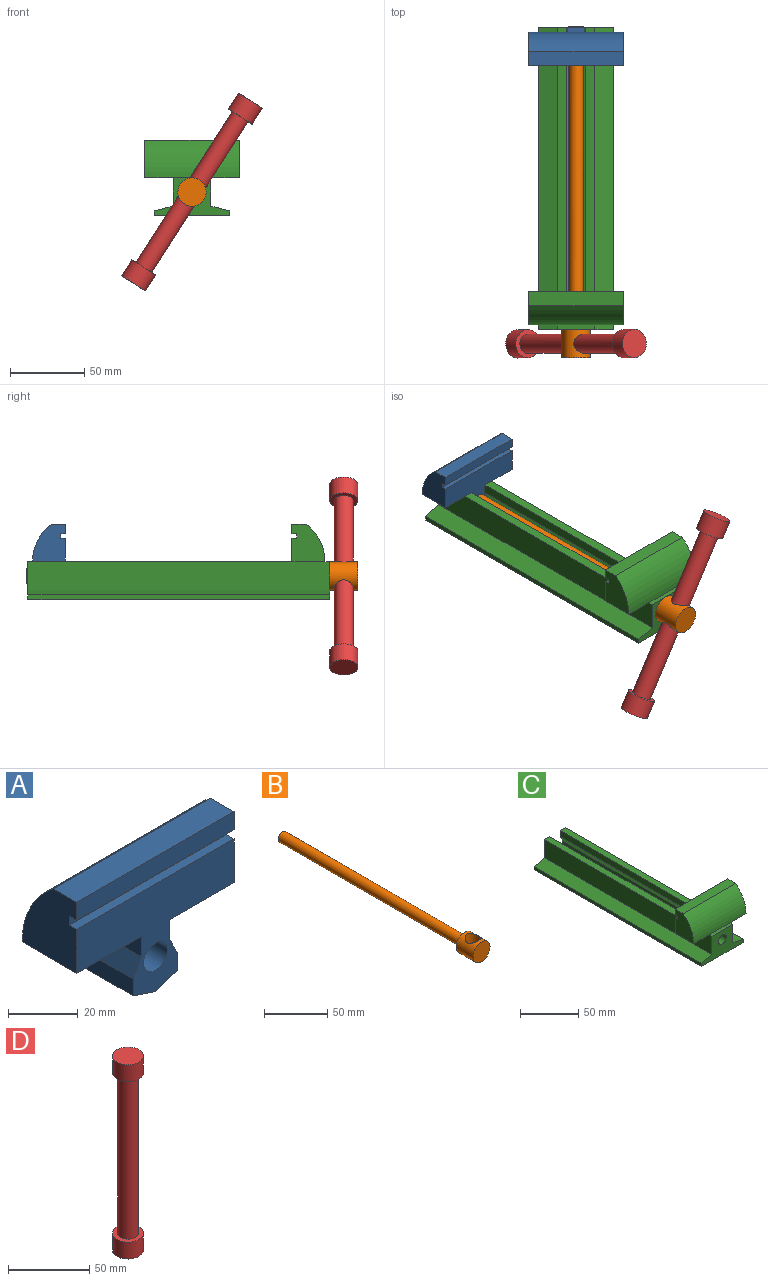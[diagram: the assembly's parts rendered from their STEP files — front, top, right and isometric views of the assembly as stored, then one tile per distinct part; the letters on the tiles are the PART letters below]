
ASSEMBLY  parts=4 mates=4
PART A: 22 faces, bbox 63.5x25.4x47.1 mm
  f0: plane 25.4x5.86mm, normal (-1,0,0), area 148.9mm2, adj f1,f8,f9,f10
  f1: plane 25.4x6.35mm, normal (-0.89,0,0.45), area 180.3mm2, adj f0,f2,f9,f10
  f2: plane 25.4x6.98mm, normal (-1,0,0), area 177.2mm2, adj f1,f3,f9,f10,f12
  f3: plane 11.68x3.18mm, normal (0,0,1), area 37.1mm2, adj f2,f4,f10,f13
  f4: plane 25.4x6.98mm, normal (1,0,0), area 177.2mm2, adj f3,f5,f9,f10,f11
  f5: plane 25.4x6.35mm, normal (0.89,0,0.45), area 180.3mm2, adj f4,f6,f9,f10
  f6: plane 25.4x5.86mm, normal (1,0,0), area 148.9mm2, adj f5,f7,f9,f10
  f7: plane 25.4x9.02mm, normal (0.32,0,-0.95), area 241.4mm2, adj f6,f8,f9,f10
  f8: plane 25.4x9.02mm, normal (-0.32,0,-0.95), area 241.4mm2, adj f0,f7,f9,f10
  f9: plane 63.5x37.56mm, normal (0,-1,0), area 1213.3mm2, adj f0,f1,f2,f4,f5,f6,f7,f8
  f10: plane 22.2x18.03mm, normal (0,1,0), area 237.5mm2, adj f0,f1,f2,f3,f4,f5,f6,f7
  f11: plane 25.91x22.23mm, normal (0,0,-1), area 575.8mm2, adj f4,f9,f13,f19
  f12: plane 25.91x22.23mm, normal (0,0,-1), area 575.8mm2, adj f2,f9,f13,f20
  f13: cylinder r=31.75mm len=63.5mm, axis (-1,0,0), area 1837.4mm2, adj f3,f11,f12,f14,f19,f20
  f14: plane 63.5x9.53mm, normal (0,0,1), area 604.8mm2, adj f13,f15,f19,f20
  f15: plane 63.5x6.35mm, normal (0,-1,0), area 403.2mm2, adj f14,f16,f19,f20
  f16: plane 63.5x3.18mm, normal (0,0,-1), area 201.6mm2, adj f15,f17,f19,f20
  f17: plane 63.5x3.18mm, normal (0,-1,0), area 201.6mm2, adj f16,f18,f19,f20
  f18: plane 63.5x3.18mm, normal (0,0,1), area 201.6mm2, adj f9,f17,f19,f20
  f19: plane 24.89x22.23mm, normal (1,0,0), area 446.1mm2, adj f9,f11,f13,f14,f15,f16,f17,f18
  f20: plane 24.89x22.23mm, normal (-1,0,0), area 446.1mm2, adj f9,f12,f13,f14,f15,f16,f17,f18
  f21: cylinder r=4.76mm len=25.4mm, axis (0,1,0), area 760.1mm2, adj f9,f10
PART B: 6 faces, bbox 19.1x223.5x19.1 mm
  f0: plane 9.53x9.53mm, normal (0,1,0), area 71.3mm2, adj f1
  f1: cylinder r=4.76mm len=204.47mm, axis (0,-1,0), area 6118.5mm2, adj f0,f4
  f2: cylinder r=9.53mm len=19.05mm, axis (0,1,0), area 869.6mm2, adj f3,f4,f5
  f3: plane 19.05x19.05mm, normal (0,-1,0), area 285mm2, adj f2
  f4: plane 19.05x19.05mm, normal (0,1,0), area 213.8mm2, adj f1,f2
  f5: cylinder r=6.35mm len=19.05mm, axis (0,0,1), area 666.8mm2, adj f2
PART C: 32 faces, bbox 63.5x203.2x50.8 mm
  f0: plane 177.8x6.35mm, normal (0,0,1), area 1129mm2, adj f6,f10,f13,f21
  f1: plane 177.8x6.35mm, normal (0,0,1), area 1129mm2, adj f8,f10,f20,f21
  f2: plane 203.2x3.18mm, normal (-1,0,0), area 645.2mm2, adj f3,f9,f10,f11
  f3: plane 203.2x50.8mm, normal (0,0,-1), area 10322.6mm2, adj f2,f4,f10,f11
  f4: plane 203.2x3.18mm, normal (1,0,0), area 645.2mm2, adj f3,f5,f10,f11
  f5: plane 203.2x12.7mm, normal (0.24,0,0.97), area 2660.1mm2, adj f4,f6,f10,f11
  f6: plane 203.2x19.05mm, normal (1,0,0), area 3871mm2, adj f0,f5,f7,f10,f11,f24
  f7: plane 25.4x3.18mm, normal (0,0,1), area 80.6mm2, adj f6,f8,f11,f23
  f8: plane 203.2x19.05mm, normal (-1,0,0), area 3871mm2, adj f1,f7,f9,f10,f11,f22
  f9: plane 203.2x12.7mm, normal (-0.24,0,0.97), area 2660.1mm2, adj f2,f8,f10,f11
  f10: plane 50.8x25.4mm, normal (0,1,0), area 433.5mm2, adj f0,f1,f2,f3,f4,f5,f6,f8
  f11: plane 50.8x25.4mm, normal (0,-1,0), area 694.9mm2, adj f2,f3,f4,f5,f6,f7,f8,f9
  f12: cylinder r=4.76mm len=25.4mm, axis (0,-1,0), area 760.1mm2, adj f11,f21
  f13: plane 177.8x6.35mm, normal (-1,0,0), area 1129mm2, adj f0,f10,f14,f21
  f14: plane 177.8x6.35mm, normal (-0.89,0,-0.45), area 1262.3mm2, adj f10,f13,f15,f21
  f15: plane 177.8x6.35mm, normal (-1,0,0), area 1129mm2, adj f10,f14,f16,f21
  f16: plane 177.8x9.53mm, normal (-0.32,0,0.95), area 1785.2mm2, adj f10,f15,f17,f21
  f17: plane 177.8x9.53mm, normal (0.32,0,0.95), area 1785.2mm2, adj f10,f16,f18,f21
  f18: plane 177.8x6.35mm, normal (1,0,0), area 1129mm2, adj f10,f17,f19,f21
  f19: plane 177.8x6.35mm, normal (0.89,0,-0.45), area 1262.3mm2, adj f10,f18,f20,f21
  f20: plane 177.8x6.35mm, normal (1,0,0), area 1129mm2, adj f1,f10,f19,f21
  f21: plane 63.5x38.1mm, normal (0,1,0), area 1269.5mm2, adj f0,f1,f12,f13,f14,f15,f16,f17
  f22: plane 22.23x19.05mm, normal (0,0,-1), area 423.4mm2, adj f8,f21,f23,f31
  f23: cylinder r=31.75mm len=63.5mm, axis (-1,0,0), area 1869.5mm2, adj f7,f22,f24,f29,f30,f31
  f24: plane 22.23x19.05mm, normal (0,0,-1), area 423.4mm2, adj f6,f21,f23,f30
  f25: plane 63.5x3.18mm, normal (0,0,1), area 201.6mm2, adj f21,f26,f30,f31
  f26: plane 63.5x3.18mm, normal (0,1,0), area 201.6mm2, adj f25,f27,f30,f31
  f27: plane 63.5x3.18mm, normal (0,0,-1), area 201.6mm2, adj f26,f28,f30,f31
  f28: plane 63.5x6.35mm, normal (0,1,0), area 403.2mm2, adj f27,f29,f30,f31
  f29: plane 63.5x9.53mm, normal (0,0,1), area 604.8mm2, adj f23,f28,f30,f31
  f30: plane 25.4x22.23mm, normal (1,0,0), area 457.3mm2, adj f21,f23,f24,f25,f26,f27,f28,f29
  f31: plane 25.4x22.23mm, normal (-1,0,0), area 457.3mm2, adj f21,f22,f23,f25,f26,f27,f28,f29
PART D: 7 faces, bbox 19.1x19.1x146.1 mm
  f0: cylinder r=6.35mm len=120.65mm, axis (0,0,-1), area 4813.7mm2, adj f3,f6
  f1: cylinder r=9.53mm len=19.05mm, axis (0,0,-1), area 760.1mm2, adj f2,f3
  f2: plane 19.05x19.05mm, normal (0,0,1), area 285mm2, adj f1
  f3: plane 19.05x19.05mm, normal (0,0,-1), area 158.3mm2, adj f0,f1
  f4: cylinder r=9.53mm len=19.05mm, axis (0,0,1), area 760.1mm2, adj f5,f6
  f5: plane 19.05x19.05mm, normal (0,0,-1), area 285mm2, adj f4
  f6: plane 19.05x19.05mm, normal (0,0,1), area 158.3mm2, adj f0,f4
PLACE A t=(0,0.12,0)mm
PLACE B rot(axis=(0,1,0),32.6deg) t=(-8.55,1.27,2.5)mm
PLACE C at identity fixed
PLACE D rot(axis=(0.74,-0.64,-0.22),158.8deg) t=(-85.18,-127.11,89.18)mm
MATE slider C.f12 <-> A.f21  axis (0,1,0) through (0,-76.2,15.88)mm
MATE revolute B.f1 <-> C.f12  axis (0,-1,0) through (0,-101.6,15.87)mm
MATE cylindrical D.f0 <-> B.f5  axis (0.54,0,0.84) through (0,-111.13,15.87)mm
MATE cylindrical B.f1 <-> A.f21  axis (0,1,0) through (0,102.87,15.88)mm
